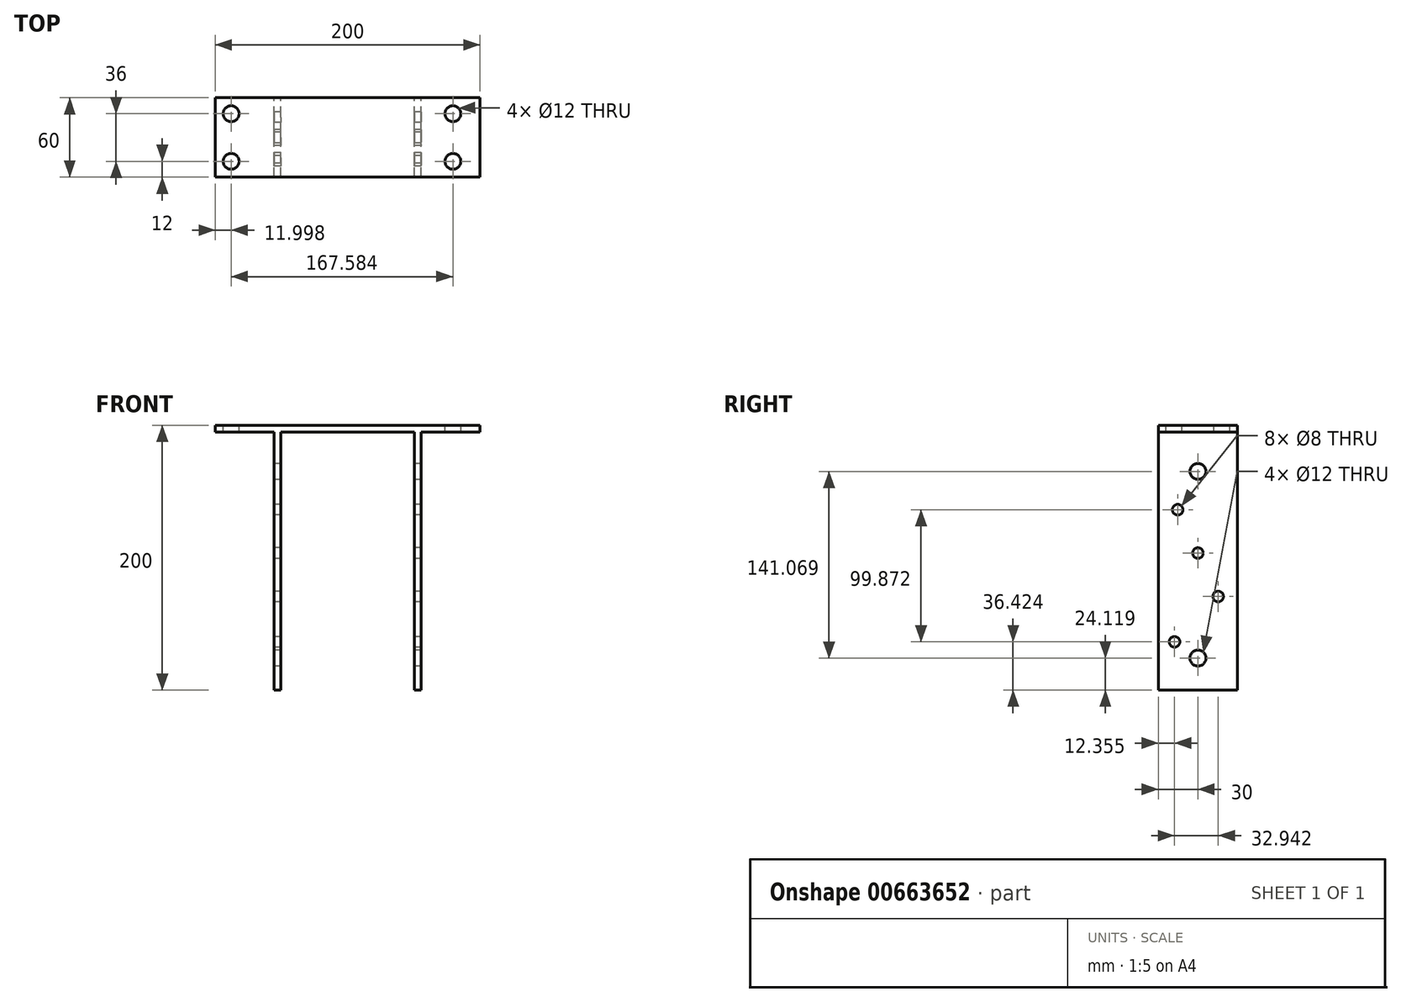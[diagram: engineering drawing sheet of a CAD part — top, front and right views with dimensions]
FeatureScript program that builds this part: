
annotation { "Feature Type Name" : "Feature", "Feature Type Description" : "" }
export const myFeature = defineFeature(function(context is Context, id is Id, definition is map)
    precondition{}
    {
        {
            var Q0;
            Q0=qCreatedBy(makeId("Front.planeOp"),FACE);
            var sketch = newSketch(context, id + "F0", { "sketchPlane" : qUnion([Q0])});
            skLineSegment(sketch, "E0.bottom", {"start": v(-95.8, 89.69) * mm, "end": v(104.2, 89.69) * mm});
            skLineSegment(sketch, "E0.top", {"start": v(-95.8, 84.69) * mm, "end": v(-51.3, 84.69) * mm});
            skLineSegment(sketch, "E0.left", {"start": v(-95.8, 89.69) * mm, "end": v(-95.8, 84.69) * mm});
            skLineSegment(sketch, "E0.right", {"start": v(104.2, 89.69) * mm, "end": v(104.2, 84.69) * mm});
            skLineSegment(sketch, "E1.top", {"start": v(-51.3, -110.31) * mm, "end": v(-46.3, -110.31) * mm});
            skLineSegment(sketch, "E1.left", {"start": v(-51.3, 84.69) * mm, "end": v(-51.3, -110.31) * mm});
            skLineSegment(sketch, "E1.right", {"start": v(-46.3, 84.69) * mm, "end": v(-46.3, -110.31) * mm});
            skLineSegment(sketch, "E2", {"start": v(4.2, 84.69) * mm, "end": v(4.2, -85.07) * mm, "construction": true});
            skLineSegment(sketch, "E3.MirrorCS", {"start": v(54.7, 84.69) * mm, "end": v(54.7, -110.31) * mm});
            skLineSegment(sketch, "E4.MirrorCS", {"start": v(59.7, 84.69) * mm, "end": v(59.7, -110.31) * mm});
            skLineSegment(sketch, "E5.MirrorCS", {"start": v(59.7, -110.31) * mm, "end": v(54.7, -110.31) * mm});
            skLineSegment(sketch, "E6.trimOffspring", {"start": v(-46.3, 84.69) * mm, "end": v(54.7, 84.69) * mm});
            skLineSegment(sketch, "E7.trimOffspring", {"start": v(59.7, 84.69) * mm, "end": v(104.2, 84.69) * mm});
            skSolve(sketch);
        }
        {
            var Q0;
            Q0=makeQuery(id+"F0.imprint","IMPRINT",FACE,{"disambiguationData":[TD([[makeQuery(id+"F0.imprint","IMPRINT",EDGE,{"derivedFrom":sQuery(id+"F0.wireOp",EDGE,"E0.bottom")}),-1.0]])]});
            extrude(context, id + "F1", {"entities" : qUnion([Q0]), "depth" : 60 * mm, "offsetDistance" : 25 * mm});
        }
        {
            var Q0;
            Q0=makeQuery(id+"F1.opExtrude","SWEPT_FACE",FACE,{"disambiguationData":[OSD([sQuery(id+"F0.wireOp",EDGE,"E0.bottom")])]});
            var sketch = newSketch(context, id + "F2", { "sketchPlane" : qUnion([Q0])});
            skCircle(sketch, "E8", {"center": v(-83.8, -12) * mm, "radius": 6 * mm});
            skLineSegment(sketch, "E9", {"start": v(-95.8, -30) * mm, "end": v(0, -30) * mm, "construction": true});
            skLineSegment(sketch, "E10", {"start": v(0, -30) * mm, "end": v(0, 0) * mm, "construction": true});
            skCircle(sketch, "E11.MirrorC", {"center": v(83.8, -12) * mm, "radius": 6 * mm});
            skCircle(sketch, "E12.MirrorC", {"center": v(-83.8, -48) * mm, "radius": 6 * mm});
            skCircle(sketch, "E13.MirrorC", {"center": v(83.8, -48) * mm, "radius": 6 * mm});
            skSolve(sketch);
        }
        {
            var Q0;
            Q0 = qSketchRegion(id + "F2", true);
            extrude(context, id + "F3", {"entities" : qUnion([Q0]), "operationType" : NewBodyOperationType.REMOVE, "oppositeDirection" : true, "depth" : 25 * mm, "offsetDistance" : 25 * mm});
        }
        {
            var Q0;
            Q0=makeQuery(id+"F1.opExtrude","SWEPT_FACE",FACE,{"disambiguationData":[OSD([sQuery(id+"F0.wireOp",EDGE,"E1.left")])]});
            var sketch = newSketch(context, id + "F4", { "sketchPlane" : qUnion([Q0])});
            skLineSegment(sketch, "E14", {"start": v(30, 84.69) * mm, "end": v(30, -110.31) * mm, "construction": true});
            skLineSegment(sketch, "E15", {"start": v(60, -12.81) * mm, "end": v(0, -12.81) * mm, "construction": true});
            skCircle(sketch, "E16", {"center": v(30, 54.88) * mm, "radius": 6 * mm});
            skCircle(sketch, "E17", {"center": v(30, -86.2) * mm, "radius": 6 * mm});
            skCircle(sketch, "E18", {"center": v(30, -6.82) * mm, "radius": 4 * mm});
            skLineSegment(sketch, "E19", {"start": v(14.7, -39.63) * mm, "end": v(45.3, 25.99) * mm, "construction": true});
            skCircle(sketch, "E20", {"center": v(14.7, -39.63) * mm, "radius": 4 * mm});
            skCircle(sketch, "E21", {"center": v(45.3, 25.99) * mm, "radius": 4 * mm});
            skCircle(sketch, "E22", {"center": v(47.64, -73.89) * mm, "radius": 4 * mm});
            skSolve(sketch);
        }
        {
            var Q0;
            Q0 = qSketchRegion(id + "F4", true);
            extrude(context, id + "F5", {"entities" : qUnion([Q0]), "operationType" : NewBodyOperationType.REMOVE, "endBound" : BoundingType.THROUGH_ALL, "oppositeDirection" : true, "depth" : 25 * mm, "offsetDistance" : 25 * mm});
        }
    });
